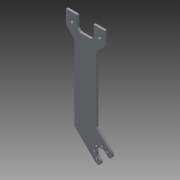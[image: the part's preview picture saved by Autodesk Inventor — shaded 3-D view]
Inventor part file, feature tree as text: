
AUTODESK INVENTOR PART (.ipt)
format: ipt  version: 2013 (Build 170138000, 138)  size: 192,000 bytes
history: native  units: mm
features: sketch x3, extrude x2, fillet x2, hole x1, pattern_circular x1
ambient origin geometry x8: Origin, YZ Plane, XZ Plane, XY Plane, X Axis, Y Axis, Z Axis, Center Point
feature tree (9):
  extrude  "押し出し2"  Depth=20.0mm
  hole  "穴1"  [1 undecoded]
  pattern_circular  "円形状パターン1"  Angle=135.0deg  [1 undecoded]
  extrude  "押し出し3"  TaperAngle=45.0deg  [1 undecoded]
  fillet  "フィレット1"  Radius=15.0mm
  fillet  "フィレット2"  Radius=2.5mm
  sketch  "スケッチ1"
  sketch  "スケッチ2"
  sketch  "スケッチ3"
note: 3 required parameter values undecoded (feature->parameter linkage not recoverable at this tier; creation-order binding heuristic only, values carry confidence <= 0.55)
